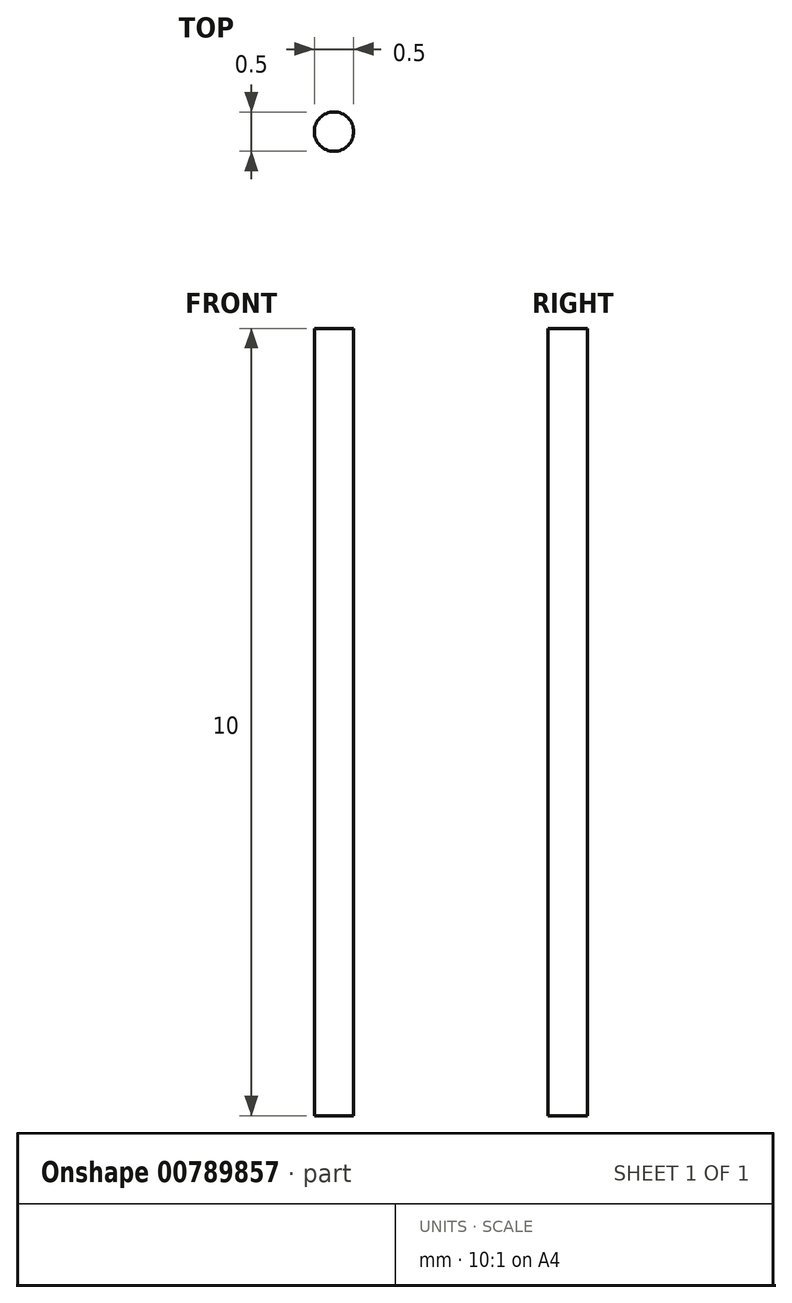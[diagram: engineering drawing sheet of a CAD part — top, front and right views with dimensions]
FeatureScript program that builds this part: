
annotation { "Feature Type Name" : "Feature", "Feature Type Description" : "" }
export const myFeature = defineFeature(function(context is Context, id is Id, definition is map)
    precondition{}
    {
        {
            var Q0;
            Q0=qCreatedBy(makeId("Top.planeOp"),FACE);
            var sketch = newSketch(context, id + "F0", { "sketchPlane" : qUnion([Q0])});
            skCircle(sketch, "E0", {"center": v(0, 0) * mm, "radius": 0.25 * mm});
            skSolve(sketch);
        }
        {
            var Q0;
            Q0=qSketchRegion(id+"F0",true);
            extrude(context, id + "F1", {"entities" : qUnion([Q0]), "depth" : 10 * mm, "offsetDistance" : 25 * mm});
        }
    });
